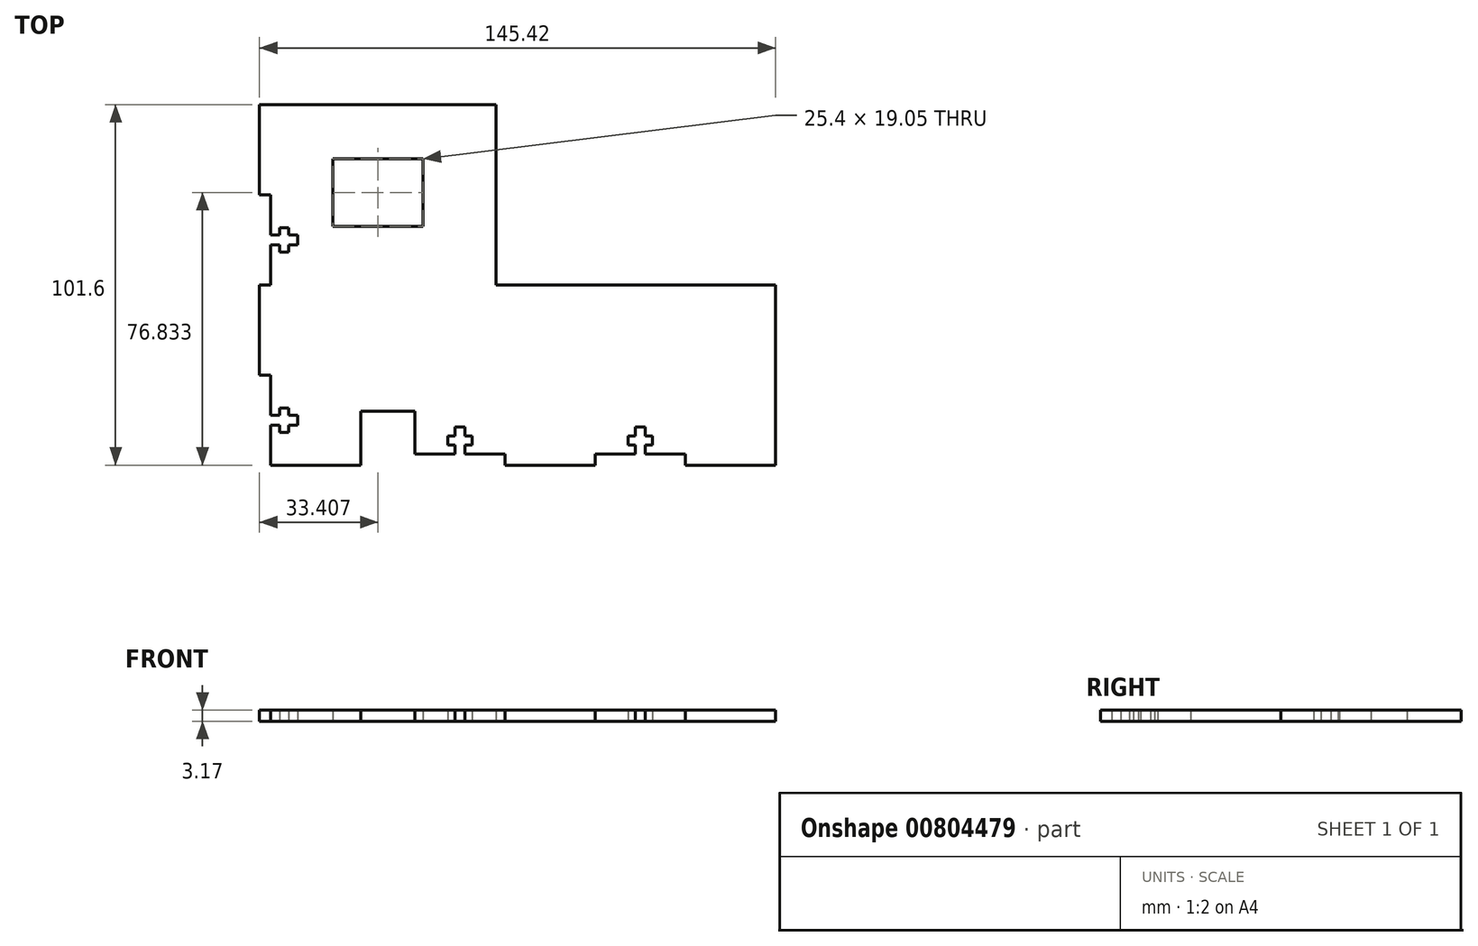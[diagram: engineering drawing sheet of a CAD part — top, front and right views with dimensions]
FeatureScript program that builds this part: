
annotation { "Feature Type Name" : "Feature", "Feature Type Description" : "" }
export const myFeature = defineFeature(function(context is Context, id is Id, definition is map)
    precondition{}
    {
        {
            var Q0;
            Q0=qCreatedBy(makeId("Top.planeOp"),FACE);
            var sketch = newSketch(context, id + "F0", { "sketchPlane" : qUnion([Q0])});
            skLineSegment(sketch, "E0.top", {"start": v(2.07, 50.6) * mm, "end": v(-61.43, 50.6) * mm});
            skLineSegment(sketch, "E0.left", {"start": v(2.07, -0.2) * mm, "end": v(2.07, 50.6) * mm});
            skLineSegment(sketch, "E1.right", {"start": v(80.8, -0.2) * mm, "end": v(80.8, -51) * mm});
            skLineSegment(sketch, "E2", {"start": v(-36.03, -51) * mm, "end": v(-36.03, -35.75) * mm});
            skLineSegment(sketch, "E3", {"start": v(55.4, -51) * mm, "end": v(55.4, -47.82) * mm});
            skLineSegment(sketch, "E4", {"start": v(30, -47.82) * mm, "end": v(55.4, -47.82) * mm});
            skLineSegment(sketch, "E5", {"start": v(30, -47.82) * mm, "end": v(30, -51) * mm});
            skLineSegment(sketch, "E6", {"start": v(-36.03, -35.75) * mm, "end": v(-20.8, -35.75) * mm});
            skLineSegment(sketch, "E7", {"start": v(-20.8, -35.75) * mm, "end": v(-20.8, -47.82) * mm});
            skLineSegment(sketch, "E8", {"start": v(4.6, -47.82) * mm, "end": v(-20.8, -47.82) * mm});
            skLineSegment(sketch, "E9", {"start": v(4.6, -47.82) * mm, "end": v(4.6, -51) * mm});
            skLineSegment(sketch, "E10", {"start": v(-60.16, -27.23) * mm, "end": v(-48.86, -27.23) * mm, "construction": true});
            skLineSegment(sketch, "E11", {"start": v(-47.33, -27.34) * mm, "end": v(-36.03, -27.34) * mm, "construction": true});
            skLineSegment(sketch, "E12", {"start": v(-61.43, 50.6) * mm, "end": v(-64.6, 50.6) * mm});
            skLineSegment(sketch, "E13", {"start": v(-64.6, 50.6) * mm, "end": v(-64.6, 25.2) * mm});
            skLineSegment(sketch, "E14", {"start": v(-64.6, 25.2) * mm, "end": v(-61.43, 25.2) * mm});
            skLineSegment(sketch, "E15.1.0.0", {"start": v(-64.6, -0.2) * mm, "end": v(-64.6, -25.6) * mm});
            skLineSegment(sketch, "E15.1.0.1", {"start": v(-61.43, -0.2) * mm, "end": v(-64.6, -0.2) * mm});
            skLineSegment(sketch, "E15.1.0.2", {"start": v(-64.6, -25.6) * mm, "end": v(-61.43, -25.6) * mm});
            skLineSegment(sketch, "E15.direction1", {"start": v(-64.6, 25.2) * mm, "end": v(-64.6, -25.6) * mm, "construction": true});
            skLineSegment(sketch, "E16.MirrorCS", {"start": v(-6.7, -42.74) * mm, "end": v(-6.7, -45.28) * mm, "construction": true});
            skLineSegment(sketch, "E17.MirrorCS", {"start": v(-9.49, -42.74) * mm, "end": v(-9.49, -45.28) * mm, "construction": true});
            skLineSegment(sketch, "E18.MirrorCS", {"start": v(-4.66, -45.28) * mm, "end": v(-4.66, -42.74) * mm});
            skLineSegment(sketch, "E19.MirrorCS", {"start": v(-11.52, -42.74) * mm, "end": v(-11.52, -45.28) * mm});
            skLineSegment(sketch, "E20.MirrorCS", {"start": v(-9.49, -45.28) * mm, "end": v(-9.49, -47.82) * mm});
            skLineSegment(sketch, "E21.MirrorCS", {"start": v(-6.7, -45.28) * mm, "end": v(-9.49, -45.28) * mm, "construction": true});
            skLineSegment(sketch, "E22.MirrorCS", {"start": v(-6.7, -47.82) * mm, "end": v(-6.7, -45.28) * mm});
            skLineSegment(sketch, "E23.MirrorCS", {"start": v(-6.7, -45.28) * mm, "end": v(-4.66, -45.28) * mm});
            skLineSegment(sketch, "E24.MirrorCS", {"start": v(-9.49, -40.2) * mm, "end": v(-9.49, -42.74) * mm});
            skLineSegment(sketch, "E25.MirrorCS", {"start": v(-4.66, -42.74) * mm, "end": v(-6.7, -42.74) * mm});
            skLineSegment(sketch, "E26.MirrorCS", {"start": v(-6.7, -42.74) * mm, "end": v(-9.49, -42.74) * mm, "construction": true});
            skLineSegment(sketch, "E27.MirrorCS", {"start": v(-6.7, -40.2) * mm, "end": v(-9.49, -40.2) * mm});
            skLineSegment(sketch, "E28.MirrorCS", {"start": v(-9.49, -42.74) * mm, "end": v(-11.52, -42.74) * mm});
            skLineSegment(sketch, "E29.MirrorCS", {"start": v(-11.52, -45.28) * mm, "end": v(-9.49, -45.28) * mm});
            skLineSegment(sketch, "E30.MirrorCS", {"start": v(-6.7, -42.74) * mm, "end": v(-6.7, -40.2) * mm});
            skLineSegment(sketch, "E31", {"start": v(-61.43, -51) * mm, "end": v(-36.03, -51) * mm});
            skLineSegment(sketch, "E32", {"start": v(4.6, -51) * mm, "end": v(30, -51) * mm});
            skLineSegment(sketch, "E33", {"start": v(55.4, -51) * mm, "end": v(80.8, -51) * mm});
            skLineSegment(sketch, "E34.1.0.0", {"start": v(46.14, -45.28) * mm, "end": v(46.14, -42.74) * mm});
            skLineSegment(sketch, "E34.1.0.1", {"start": v(44.1, -40.2) * mm, "end": v(41.31, -40.2) * mm});
            skLineSegment(sketch, "E34.1.0.2", {"start": v(39.28, -45.28) * mm, "end": v(41.31, -45.28) * mm});
            skLineSegment(sketch, "E34.1.0.3", {"start": v(41.31, -42.74) * mm, "end": v(39.28, -42.74) * mm});
            skLineSegment(sketch, "E34.1.0.4", {"start": v(44.1, -42.74) * mm, "end": v(44.1, -40.2) * mm});
            skLineSegment(sketch, "E34.1.0.5", {"start": v(39.28, -42.74) * mm, "end": v(39.28, -45.28) * mm});
            skLineSegment(sketch, "E34.1.0.6", {"start": v(44.1, -45.28) * mm, "end": v(41.31, -45.28) * mm, "construction": true});
            skLineSegment(sketch, "E34.1.0.7", {"start": v(46.14, -42.74) * mm, "end": v(44.1, -42.74) * mm});
            skLineSegment(sketch, "E34.1.0.8", {"start": v(44.1, -42.74) * mm, "end": v(41.31, -42.74) * mm, "construction": true});
            skLineSegment(sketch, "E34.1.0.9", {"start": v(41.31, -42.74) * mm, "end": v(41.31, -45.28) * mm, "construction": true});
            skLineSegment(sketch, "E34.1.0.10", {"start": v(44.1, -42.74) * mm, "end": v(44.1, -45.28) * mm, "construction": true});
            skLineSegment(sketch, "E34.1.0.11", {"start": v(44.1, -45.28) * mm, "end": v(46.14, -45.28) * mm});
            skLineSegment(sketch, "E34.1.0.12", {"start": v(41.31, -40.2) * mm, "end": v(41.31, -42.74) * mm});
            skLineSegment(sketch, "E34.1.0.13", {"start": v(41.31, -45.28) * mm, "end": v(41.31, -47.82) * mm});
            skLineSegment(sketch, "E34.1.0.14", {"start": v(44.1, -47.82) * mm, "end": v(44.1, -45.28) * mm});
            skLineSegment(sketch, "E34.direction1", {"start": v(-9.49, -47.82) * mm, "end": v(41.31, -47.82) * mm, "construction": true});
            skLineSegment(sketch, "E35.MirrorCS", {"start": v(-56.35, 11.11) * mm, "end": v(-58.9, 11.11) * mm, "construction": true});
            skLineSegment(sketch, "E36.MirrorCS", {"start": v(-56.35, 13.9) * mm, "end": v(-58.9, 13.9) * mm, "construction": true});
            skLineSegment(sketch, "E37.MirrorCS", {"start": v(-58.9, 9.08) * mm, "end": v(-56.35, 9.08) * mm});
            skLineSegment(sketch, "E38.MirrorCS", {"start": v(-56.35, 15.94) * mm, "end": v(-58.9, 15.94) * mm});
            skLineSegment(sketch, "E39.MirrorCS", {"start": v(-58.9, 13.9) * mm, "end": v(-61.43, 13.9) * mm});
            skLineSegment(sketch, "E40.MirrorCS", {"start": v(-58.9, 11.11) * mm, "end": v(-58.9, 13.9) * mm, "construction": true});
            skLineSegment(sketch, "E41.MirrorCS", {"start": v(-61.43, 11.11) * mm, "end": v(-58.9, 11.11) * mm});
            skLineSegment(sketch, "E42.MirrorCS", {"start": v(-58.9, 11.11) * mm, "end": v(-58.9, 9.08) * mm});
            skLineSegment(sketch, "E43.MirrorCS", {"start": v(-53.81, 13.9) * mm, "end": v(-56.35, 13.9) * mm});
            skLineSegment(sketch, "E44.MirrorCS", {"start": v(-56.35, 9.08) * mm, "end": v(-56.35, 11.11) * mm});
            skLineSegment(sketch, "E45.MirrorCS", {"start": v(-56.35, 11.11) * mm, "end": v(-56.35, 13.9) * mm, "construction": true});
            skLineSegment(sketch, "E46.MirrorCS", {"start": v(-53.81, 11.11) * mm, "end": v(-53.81, 13.9) * mm});
            skLineSegment(sketch, "E47.MirrorCS", {"start": v(-56.35, 13.9) * mm, "end": v(-56.35, 15.94) * mm});
            skLineSegment(sketch, "E48.MirrorCS", {"start": v(-58.9, 15.94) * mm, "end": v(-58.9, 13.9) * mm});
            skLineSegment(sketch, "E49.MirrorCS", {"start": v(-56.35, 11.11) * mm, "end": v(-53.81, 11.11) * mm});
            skLineSegment(sketch, "E50", {"start": v(-61.43, 25.2) * mm, "end": v(-61.43, -0.2) * mm});
            skLineSegment(sketch, "E51", {"start": v(-61.43, -25.6) * mm, "end": v(-61.43, -51) * mm});
            skLineSegment(sketch, "E52.1.0.0", {"start": v(-56.35, -39.69) * mm, "end": v(-56.35, -36.9) * mm, "construction": true});
            skLineSegment(sketch, "E52.1.0.1", {"start": v(-56.35, -41.72) * mm, "end": v(-56.35, -39.69) * mm});
            skLineSegment(sketch, "E52.1.0.2", {"start": v(-56.35, -36.9) * mm, "end": v(-58.9, -36.9) * mm, "construction": true});
            skLineSegment(sketch, "E52.1.0.3", {"start": v(-58.9, -39.69) * mm, "end": v(-58.9, -36.9) * mm, "construction": true});
            skLineSegment(sketch, "E52.1.0.4", {"start": v(-53.81, -36.9) * mm, "end": v(-56.35, -36.9) * mm});
            skLineSegment(sketch, "E52.1.0.5", {"start": v(-58.9, -41.72) * mm, "end": v(-56.35, -41.72) * mm});
            skLineSegment(sketch, "E52.1.0.6", {"start": v(-58.9, -34.86) * mm, "end": v(-58.9, -36.9) * mm});
            skLineSegment(sketch, "E52.1.0.7", {"start": v(-56.35, -39.69) * mm, "end": v(-58.9, -39.69) * mm, "construction": true});
            skLineSegment(sketch, "E52.1.0.8", {"start": v(-56.35, -34.86) * mm, "end": v(-58.9, -34.86) * mm});
            skLineSegment(sketch, "E52.1.0.9", {"start": v(-58.9, -36.9) * mm, "end": v(-61.43, -36.9) * mm});
            skLineSegment(sketch, "E52.1.0.10", {"start": v(-56.35, -39.69) * mm, "end": v(-53.81, -39.69) * mm});
            skLineSegment(sketch, "E52.1.0.11", {"start": v(-53.81, -39.69) * mm, "end": v(-53.81, -36.9) * mm});
            skLineSegment(sketch, "E52.1.0.12", {"start": v(-61.43, -39.69) * mm, "end": v(-58.9, -39.69) * mm});
            skLineSegment(sketch, "E52.1.0.13", {"start": v(-58.9, -39.69) * mm, "end": v(-58.9, -41.72) * mm});
            skLineSegment(sketch, "E52.1.0.14", {"start": v(-56.35, -36.9) * mm, "end": v(-56.35, -34.86) * mm});
            skLineSegment(sketch, "E52.direction1", {"start": v(-61.43, 11.11) * mm, "end": v(-61.43, -39.69) * mm, "construction": true});
            skLineSegment(sketch, "E53", {"start": v(2.07, -0.2) * mm, "end": v(80.8, -0.2) * mm});
            skLineSegment(sketch, "E54.bottom", {"start": v(-18.5, 16.32) * mm, "end": v(-43.9, 16.32) * mm});
            skLineSegment(sketch, "E54.top", {"start": v(-18.5, 35.37) * mm, "end": v(-43.9, 35.37) * mm});
            skLineSegment(sketch, "E54.left", {"start": v(-18.5, 16.32) * mm, "end": v(-18.5, 35.37) * mm});
            skLineSegment(sketch, "E54.right", {"start": v(-43.9, 16.32) * mm, "end": v(-43.9, 35.37) * mm});
            skPoint(sketch, "E54.middle", {"position": v(-31.2, 25.84) * mm});
            skSolve(sketch);
        }
        {
            var Q0;
            {var subQ11=sQuery(id+"F0.wireOp",EDGE,"E1.left");Q0=makeQuery(id+"F0.imprint","IMPRINT",FACE,{"disambiguationData":[TD([[makeQuery(id+"F0.imprint","IMPRINT",EDGE,{"derivedFrom":subQ11}),1.0]])]});}
            var Q1;
            Q1=makeQuery(id+"F0.imprint","IMPRINT",FACE,{"disambiguationData":[TD([[makeQuery(id+"F0.imprint","IMPRINT",EDGE,{"derivedFrom":sQuery(id+"F0.wireOp",EDGE,"E0.top")}),1.0]])]});
            var Q2;
            {var subQ0=sQuery(id+"F0.wireOp",EDGE,"E12");Q2=makeQuery(id+"F0.imprint","IMPRINT",FACE,{"disambiguationData":[TD([[makeQuery(id+"F0.imprint","IMPRINT",EDGE,{"derivedFrom":subQ0}),1.0]])]});}
            var Q3;
            Q3=makeQuery(id+"F0.imprint","IMPRINT",FACE,{"disambiguationData":[TD([[makeQuery(id+"F0.imprint","IMPRINT",EDGE,{"derivedFrom":sQuery(id+"F0.wireOp",EDGE,"E15.1.0.0")}),1.0]])]});
            extrude(context, id + "F1", {"entities" : qUnion([Q0, Q1, Q2, Q3]), "depth" : 3.17 * mm, "offsetDistance" : 25.4 * mm});
        }
    });
